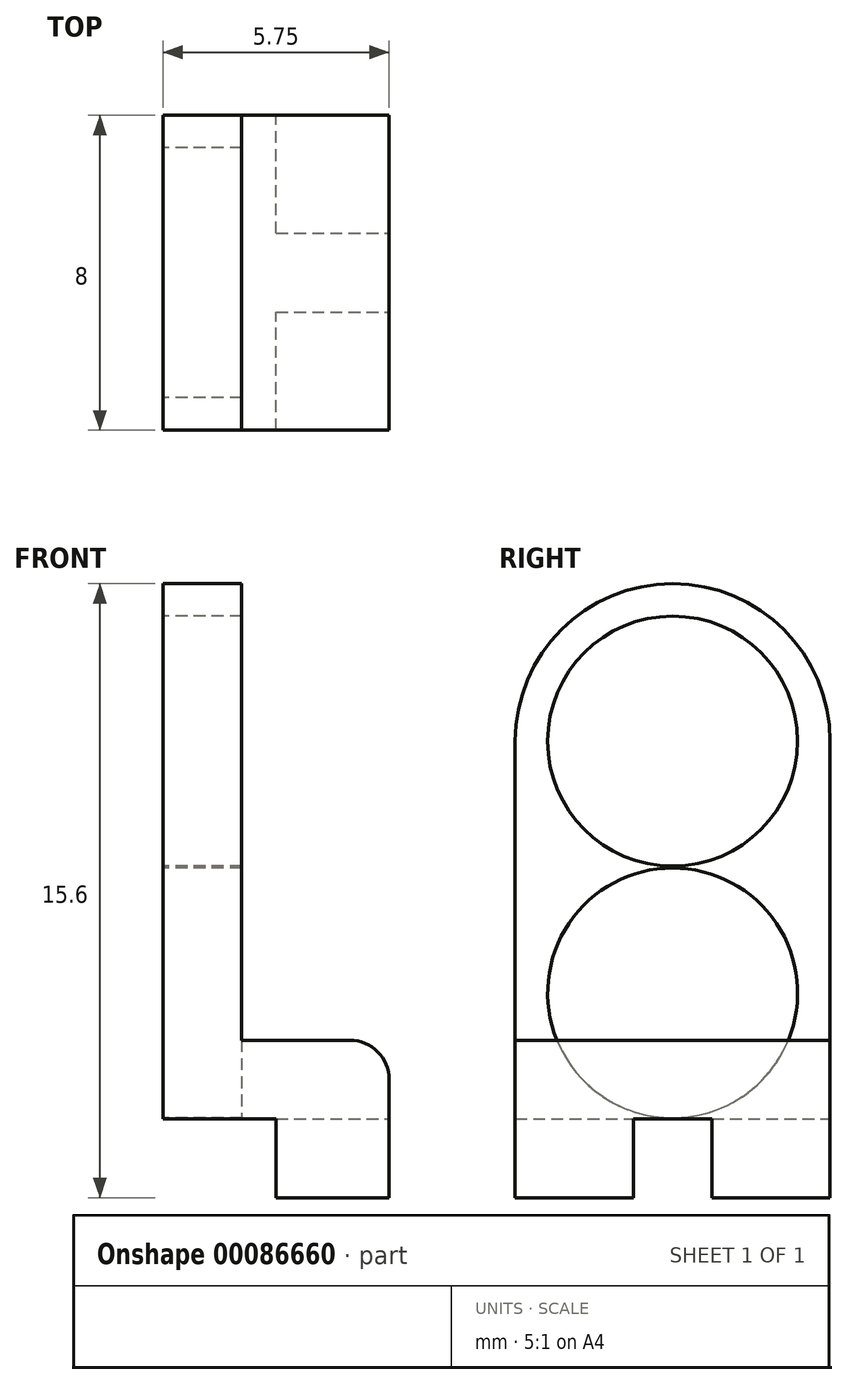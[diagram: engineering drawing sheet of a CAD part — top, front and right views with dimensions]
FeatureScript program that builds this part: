
annotation { "Feature Type Name" : "Feature", "Feature Type Description" : "" }
export const myFeature = defineFeature(function(context is Context, id is Id, definition is map)
    precondition{}
    {
        {
            var Q0;
            Q0=qCreatedBy(makeId("Right.planeOp"),FACE);
            var sketch = newSketch(context, id + "F0", { "sketchPlane" : qUnion([Q0])});
            skCircle(sketch, "E0", {"center": v(0, 9.6) * mm, "radius": 4 * mm});
            skLineSegment(sketch, "E1.bottom", {"start": v(-4, 9.6) * mm, "end": v(4, 9.6) * mm});
            skLineSegment(sketch, "E1.top", {"start": v(-4, 0) * mm, "end": v(4, 0) * mm});
            skLineSegment(sketch, "E1.left", {"start": v(-4, 9.6) * mm, "end": v(-4, 0) * mm});
            skLineSegment(sketch, "E1.right", {"start": v(4, 9.6) * mm, "end": v(4, 0) * mm});
            skSolve(sketch);
        }
        {
            var Q0;
            {var subQ0=sQuery(id+"F0.wireOp",EDGE,"E1.bottom");Q0=makeQuery(id+"F0.imprint","IMPRINT",FACE,{"disambiguationData":[TD([[makeQuery(id+"F0.imprint","IMPRINT",EDGE,{"derivedFrom":subQ0}),1.0]])]});}
            var Q1;
            {var subQ0=sQuery(id+"F0.wireOp",EDGE,"E1.bottom");Q1=makeQuery(id+"F0.imprint","IMPRINT",FACE,{"disambiguationData":[TD([[makeQuery(id+"F0.imprint","IMPRINT",EDGE,{"derivedFrom":subQ0}),-1.0]])]});}
            var Q2;
            Q2=makeQuery(id+"F0.imprint","IMPRINT",FACE,{"disambiguationData":[TD([[makeQuery(id+"F0.imprint","IMPRINT",EDGE,{"derivedFrom":sQuery(id+"F0.wireOp",EDGE,"E1.top")}),1.0]])]});
            extrude(context, id + "F1", {"entities" : qUnion([Q0, Q1, Q2]), "depth" : 2 * mm});
        }
        {
            var Q0;
            Q0=makeQuery(id+"F1.opExtrude","CAP_FACE",FACE,{"disambiguationData":[OSD([sQuery(id+"F0.wireOp",EDGE,"E0"),sQuery(id+"F0.wireOp",EDGE,"E1.top"),sQuery(id+"F0.wireOp",EDGE,"E1.left"),sQuery(id+"F0.wireOp",EDGE,"E1.right")])],"isStart":false});
            var sketch = newSketch(context, id + "F2", { "sketchPlane" : qUnion([Q0])});
            skLineSegment(sketch, "E2.bottom", {"start": v(-4, 0) * mm, "end": v(4, 0) * mm});
            skLineSegment(sketch, "E2.top", {"start": v(-4, 2) * mm, "end": v(4, 2) * mm});
            skLineSegment(sketch, "E2.left", {"start": v(-4, 0) * mm, "end": v(-4, 2) * mm});
            skLineSegment(sketch, "E2.right", {"start": v(4, 0) * mm, "end": v(4, 2) * mm});
            skSolve(sketch);
        }
        {
            var Q0;
            Q0=makeQuery(id+"F2.imprint","IMPRINT",FACE,{"disambiguationData":[TD([[makeQuery(id+"F2.imprint","IMPRINT",EDGE,{"derivedFrom":sQuery(id+"F2.wireOp",EDGE,"E2.bottom")}),1.0]])]});
            extrude(context, id + "F3", {"entities" : qUnion([Q0]), "operationType" : NewBodyOperationType.ADD, "depth" : 3.75 * mm});
        }
        {
            var Q0;
            Q0=makeQuery(id+"F3.boolean.opBoolean","MERGE",FACE,{"derivedFrom":[makeQuery(id+"F1.opExtrude","SWEPT_FACE",FACE,{"disambiguationData":[OSD([sQuery(id+"F0.wireOp",EDGE,"E1.top")])]}),makeQuery(id+"F3.opExtrude","SWEPT_FACE",FACE,{"disambiguationData":[OSD([sQuery(id+"F2.wireOp",EDGE,"E2.bottom")])]})]});
            var sketch = newSketch(context, id + "F4", { "sketchPlane" : qUnion([Q0])});
            skLineSegment(sketch, "E3.bottom", {"start": v(5.75, 4) * mm, "end": v(2.87, 4) * mm});
            skLineSegment(sketch, "E3.top", {"start": v(5.75, -4) * mm, "end": v(2.88, -4) * mm});
            skLineSegment(sketch, "E3.left", {"start": v(5.75, 4) * mm, "end": v(5.75, -4) * mm});
            skLineSegment(sketch, "E3.right", {"start": v(2.87, 4) * mm, "end": v(2.88, -4) * mm});
            skSolve(sketch);
        }
        {
            var Q0;
            Q0=makeQuery(id+"F4.imprint","IMPRINT",FACE,{"disambiguationData":[TD([[makeQuery(id+"F4.imprint","IMPRINT",EDGE,{"derivedFrom":sQuery(id+"F4.wireOp",EDGE,"E3.bottom")}),1.0]])]});
            extrude(context, id + "F5", {"entities" : qUnion([Q0]), "operationType" : NewBodyOperationType.ADD, "depth" : 2 * mm});
        }
        {
            var Q0;
            Q0=makeQuery(id+"F5.boolean.opBoolean","MERGE",FACE,{"derivedFrom":[makeQuery(id+"F3.opExtrude","CAP_FACE",FACE,{"disambiguationData":[OSD([sQuery(id+"F2.wireOp",EDGE,"E2.bottom"),sQuery(id+"F2.wireOp",EDGE,"E2.top"),sQuery(id+"F2.wireOp",EDGE,"E2.left"),sQuery(id+"F2.wireOp",EDGE,"E2.right")])],"isStart":false}),makeQuery(id+"F5.opExtrude","SWEPT_FACE",FACE,{"disambiguationData":[OSD([sQuery(id+"F4.wireOp",EDGE,"E3.left")])]})]});
            var sketch = newSketch(context, id + "F6", { "sketchPlane" : qUnion([Q0])});
            skLineSegment(sketch, "E4.bottom", {"start": v(-1, -2) * mm, "end": v(1, -2) * mm});
            skLineSegment(sketch, "E4.top", {"start": v(-1, 0) * mm, "end": v(1, 0) * mm});
            skLineSegment(sketch, "E4.left", {"start": v(-1, -2) * mm, "end": v(-1, 0) * mm});
            skLineSegment(sketch, "E4.right", {"start": v(1, -2) * mm, "end": v(1, 0) * mm});
            skSolve(sketch);
        }
        {
            var Q0;
            Q0=makeQuery(id+"F6.imprint","IMPRINT",FACE,{"disambiguationData":[TD([[makeQuery(id+"F6.imprint","IMPRINT",EDGE,{"derivedFrom":sQuery(id+"F6.wireOp",EDGE,"E4.bottom")}),1.0]])]});
            extrude(context, id + "F7", {"entities" : qUnion([Q0]), "operationType" : NewBodyOperationType.REMOVE, "oppositeDirection" : true, "depth" : 25 * mm});
        }
        {
            var Q0;
            Q0=makeQuery(id+"F1.opExtrude","CAP_FACE",FACE,{"disambiguationData":[OSD([sQuery(id+"F0.wireOp",EDGE,"E0"),sQuery(id+"F0.wireOp",EDGE,"E1.top"),sQuery(id+"F0.wireOp",EDGE,"E1.left"),sQuery(id+"F0.wireOp",EDGE,"E1.right")])],"isStart":true});
            var sketch = newSketch(context, id + "F8", { "sketchPlane" : qUnion([Q0])});
            skCircle(sketch, "E5", {"center": v(0, 9.6) * mm, "radius": 3.17 * mm});
            skSolve(sketch);
        }
        {
            var Q0;
            Q0=makeQuery(id+"F8.imprint","IMPRINT",FACE,{"disambiguationData":[TD([[makeQuery(id+"F8.imprint","IMPRINT",EDGE,{"derivedFrom":sQuery(id+"F8.wireOp",EDGE,"E5")}),1.0]])]});
            extrude(context, id + "F9", {"entities" : qUnion([Q0]), "operationType" : NewBodyOperationType.REMOVE, "oppositeDirection" : true, "depth" : 2 * mm});
        }
        {
            var Q0;
            Q0=makeQuery(id+"F1.opExtrude","CAP_FACE",FACE,{"disambiguationData":[OSD([sQuery(id+"F0.wireOp",EDGE,"E0"),sQuery(id+"F0.wireOp",EDGE,"E1.top"),sQuery(id+"F0.wireOp",EDGE,"E1.left"),sQuery(id+"F0.wireOp",EDGE,"E1.right")])],"isStart":true});
            var sketch = newSketch(context, id + "F10", { "sketchPlane" : qUnion([Q0])});
            skCircle(sketch, "E6", {"center": v(0, 3.2) * mm, "radius": 3.17 * mm});
            skSolve(sketch);
        }
        {
            var Q0;
            {var subQ0=sQuery(id+"F10.wireOp",EDGE,"E6");var subQ1=makeQuery(id+"F1.opExtrude","CAP_EDGE",EDGE,{"disambiguationData":[OSD([sQuery(id+"F0.wireOp",EDGE,"E1.top")])],"isStart":true});var subQ2=makeQuery(id+"F10.imprint","INTERSECT",VERTEX,{"disambiguationData":[OD(0.0)],"derivedFrom":[subQ1,subQ0]});Q0=makeQuery(id+"F10.imprint","IMPRINT",FACE,{"disambiguationData":[TD([[makeQuery(id+"F10.imprint","IMPRINT",EDGE,{"disambiguationData":[TD([[subQ2,-1.0]])],"derivedFrom":subQ0}),1.0]])]});}
            extrude(context, id + "F11", {"entities" : qUnion([Q0]), "operationType" : NewBodyOperationType.REMOVE, "oppositeDirection" : true, "depth" : 2 * mm});
        }
        {
            var Q0;
            Q0=makeQuery(id+"F3.opExtrude","CAP_EDGE",EDGE,{"disambiguationData":[OSD([sQuery(id+"F2.wireOp",EDGE,"E2.top")])],"isStart":false});
            fillet(context, id + "F12", {"entities" : qUnion([Q0]), "radius" : 1 * mm, "tangentPropagation" : true, "allowEdgeOverflow" : false});
        }
    });
